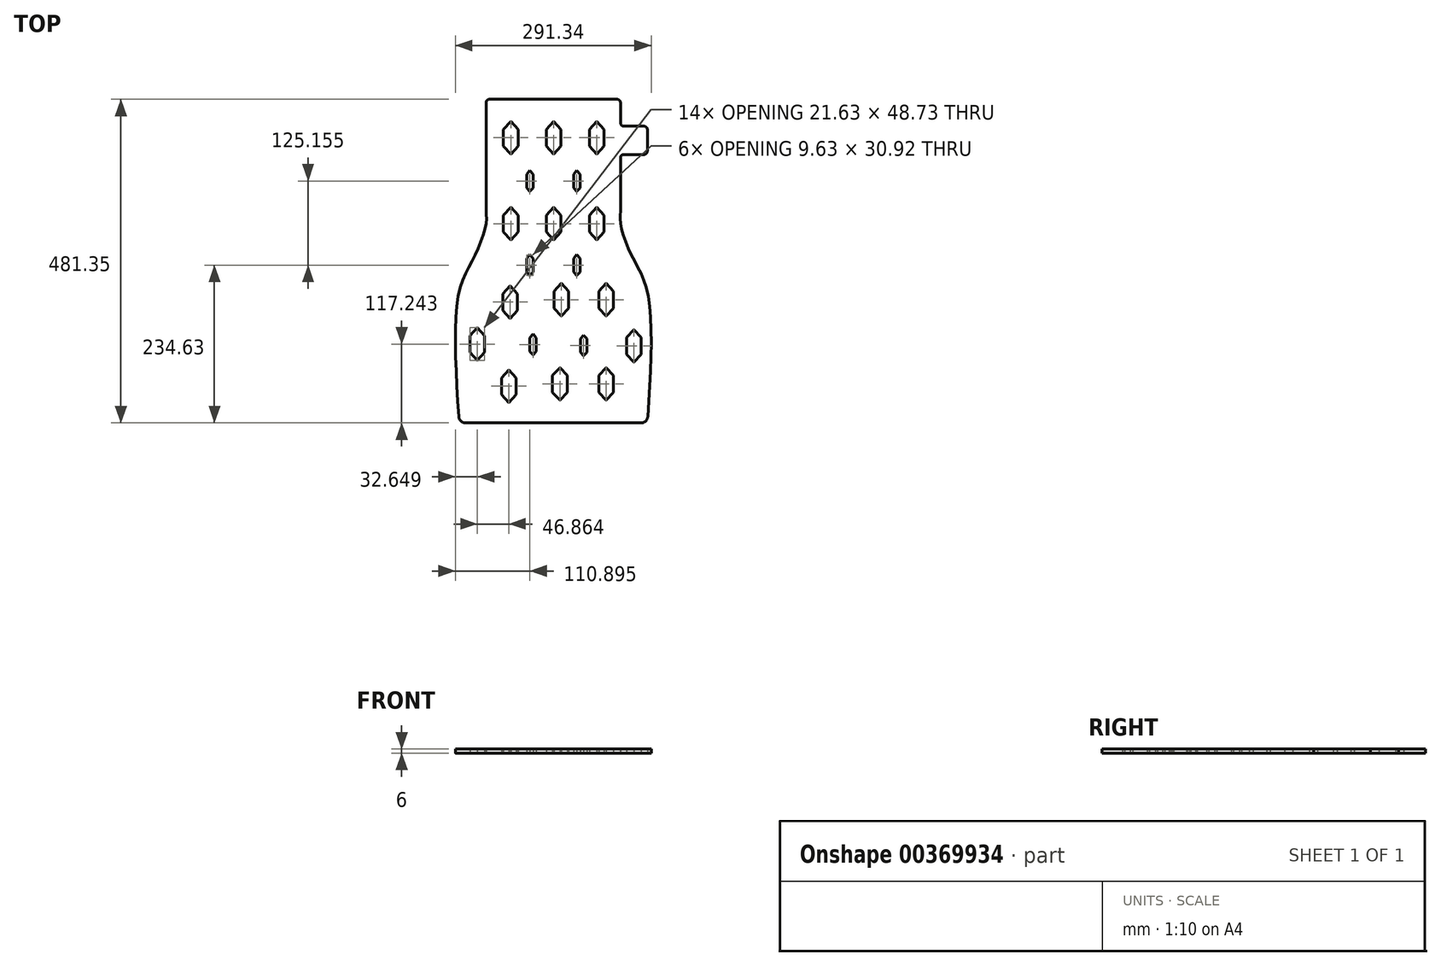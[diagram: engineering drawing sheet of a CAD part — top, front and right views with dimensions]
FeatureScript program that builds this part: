
annotation { "Feature Type Name" : "Feature", "Feature Type Description" : "" }
export const myFeature = defineFeature(function(context is Context, id is Id, definition is map)
    precondition{}
    {
        {
            var Q0;
            Q0=qCreatedBy(makeId("Top.planeOp"),FACE);
            var sketch = newSketch(context, id + "F0", { "sketchPlane" : qUnion([Q0])});
            skLineSegment(sketch, "E0", {"start": v(0, 262.18) * mm, "end": v(95, 262.18) * mm});
            skLineSegment(sketch, "E1", {"start": v(0, 262.18) * mm, "end": v(-95, 262.18) * mm});
            skLineSegment(sketch, "E2", {"start": v(130.62, -219.17) * mm, "end": v(-130.62, -219.17) * mm});
            skFitSpline(sketch, "E3", {"points": [v(-140, -219.17) * mm, v(-140, -23.78) * mm, v(-116.25, 30.48) * mm, v(-100, 77.75) * mm, v(-100, 95.38) * mm], "startDerivative": vector(-34.72, 539.25) * mm, "endDerivative": vector(-13.07, 120.29) * mm});
            skFitSpline(sketch, "E4.MirrorCS", {"points": [v(140, -219.17) * mm, v(140, -23.78) * mm, v(116.25, 30.48) * mm, v(100, 77.75) * mm, v(100, 95.38) * mm], "startDerivative": vector(34.72, 539.25) * mm, "endDerivative": vector(13.07, 120.29) * mm});
            skLineSegment(sketch, "E5", {"start": v(-100, 257.18) * mm, "end": v(-100, 95.38) * mm});
            skLineSegment(sketch, "E6", {"start": v(100, 95.38) * mm, "end": v(100, 175.09) * mm});
            skPoint(sketch, "E7.visualSharp", {"position": v(-100, 262.18) * mm});
            skArc(sketch, "E7.filletArc", {"start": v(-95, 262.18) * mm, "mid": v(-98.54, 260.72) * mm, "end": v(-100, 257.18) * mm});
            skPoint(sketch, "E8.visualSharp", {"position": v(100, 262.18) * mm});
            skArc(sketch, "E8.filletArc", {"start": v(100, 257.18) * mm, "mid": v(98.54, 260.72) * mm, "end": v(95, 262.18) * mm});
            skLineSegment(sketch, "E9", {"start": v(100, 262.18) * mm, "end": v(100, 227.18) * mm});
            skLineSegment(sketch, "E10", {"start": v(105, 222.18) * mm, "end": v(135, 222.18) * mm});
            skLineSegment(sketch, "E11", {"start": v(140, 217.18) * mm, "end": v(140, 185.09) * mm});
            skLineSegment(sketch, "E12", {"start": v(135, 180.09) * mm, "end": v(105, 180.09) * mm});
            skArc(sketch, "E13.filletArc", {"start": v(105, 180.09) * mm, "mid": v(101.46, 178.62) * mm, "end": v(100, 175.09) * mm});
            skPoint(sketch, "E14.visualSharp", {"position": v(140, 180.09) * mm});
            skArc(sketch, "E14.filletArc", {"start": v(135, 180.09) * mm, "mid": v(138.54, 181.55) * mm, "end": v(140, 185.09) * mm});
            skPoint(sketch, "E15.visualSharp", {"position": v(140, 222.18) * mm});
            skArc(sketch, "E15.filletArc", {"start": v(140, 217.18) * mm, "mid": v(138.54, 220.72) * mm, "end": v(135, 222.18) * mm});
            skPoint(sketch, "E16.visualSharp", {"position": v(100, 222.18) * mm});
            skArc(sketch, "E16.filletArc", {"start": v(100, 227.18) * mm, "mid": v(101.46, 223.65) * mm, "end": v(105, 222.18) * mm});
            skArc(sketch, "E17.filletArc", {"start": v(130.62, -219.17) * mm, "mid": v(137.46, -216.46) * mm, "end": v(140.6, -209.8) * mm});
            skArc(sketch, "E18.filletArc", {"start": v(-140.6, -209.8) * mm, "mid": v(-137.46, -216.46) * mm, "end": v(-130.62, -219.17) * mm});
            skLineSegment(sketch, "E19.left", {"start": v(-52.46, 217.58) * mm, "end": v(-52.46, 192.58) * mm});
            skLineSegment(sketch, "E19.right", {"start": v(-74.1, 217.58) * mm, "end": v(-74.1, 192.58) * mm});
            skPoint(sketch, "E20.endSnap0", {"position": v(-63.28, 136.49) * mm});
            skLineSegment(sketch, "E21", {"start": v(-63.28, 180.7) * mm, "end": v(-52.46, 192.58) * mm});
            skPoint(sketch, "E22.endSnap0", {"position": v(46.38, 56.52) * mm});
            skLineSegment(sketch, "E23.MirrorCS", {"start": v(-63.28, 229.44) * mm, "end": v(-52.46, 217.58) * mm});
            skLineSegment(sketch, "E24.MirrorCS", {"start": v(-74.1, 217.58) * mm, "end": v(-63.28, 229.44) * mm});
            skLineSegment(sketch, "E25.0.1.0", {"start": v(-74.1, 89.58) * mm, "end": v(-63.28, 101.44) * mm});
            skLineSegment(sketch, "E25.0.1.1", {"start": v(-74.1, 89.58) * mm, "end": v(-74.1, 64.58) * mm});
            skLineSegment(sketch, "E25.0.1.2", {"start": v(-74.1, 64.58) * mm, "end": v(-63.28, 52.7) * mm});
            skLineSegment(sketch, "E25.0.1.3", {"start": v(-63.28, 52.7) * mm, "end": v(-52.46, 64.58) * mm});
            skLineSegment(sketch, "E25.0.1.4", {"start": v(-52.46, 89.58) * mm, "end": v(-52.46, 64.58) * mm});
            skLineSegment(sketch, "E25.0.1.5", {"start": v(-63.28, 101.44) * mm, "end": v(-52.46, 89.58) * mm});
            skLineSegment(sketch, "E25.1.0.0", {"start": v(-10.1, 217.58) * mm, "end": v(0.72, 229.44) * mm});
            skLineSegment(sketch, "E25.1.0.1", {"start": v(-10.1, 217.58) * mm, "end": v(-10.1, 192.58) * mm});
            skLineSegment(sketch, "E25.1.0.2", {"start": v(-10.1, 192.58) * mm, "end": v(0.72, 180.7) * mm});
            skLineSegment(sketch, "E25.1.0.3", {"start": v(0.72, 180.7) * mm, "end": v(11.54, 192.58) * mm});
            skLineSegment(sketch, "E25.1.0.4", {"start": v(11.54, 217.58) * mm, "end": v(11.54, 192.58) * mm});
            skLineSegment(sketch, "E25.1.0.5", {"start": v(0.72, 229.44) * mm, "end": v(11.54, 217.58) * mm});
            skLineSegment(sketch, "E25.1.1.0", {"start": v(-10.1, 89.58) * mm, "end": v(0.72, 101.44) * mm});
            skLineSegment(sketch, "E25.1.1.1", {"start": v(-10.1, 89.58) * mm, "end": v(-10.1, 64.58) * mm});
            skLineSegment(sketch, "E25.1.1.2", {"start": v(-10.1, 64.58) * mm, "end": v(0.72, 52.7) * mm});
            skLineSegment(sketch, "E25.1.1.3", {"start": v(0.72, 52.7) * mm, "end": v(11.54, 64.58) * mm});
            skLineSegment(sketch, "E25.1.1.4", {"start": v(11.54, 89.58) * mm, "end": v(11.54, 64.58) * mm});
            skLineSegment(sketch, "E25.1.1.5", {"start": v(0.72, 101.44) * mm, "end": v(11.54, 89.58) * mm});
            skLineSegment(sketch, "E25.2.0.0", {"start": v(53.9, 217.58) * mm, "end": v(64.72, 229.44) * mm});
            skLineSegment(sketch, "E25.2.0.1", {"start": v(53.9, 217.58) * mm, "end": v(53.9, 192.58) * mm});
            skLineSegment(sketch, "E25.2.0.2", {"start": v(53.9, 192.58) * mm, "end": v(64.72, 180.7) * mm});
            skLineSegment(sketch, "E25.2.0.3", {"start": v(64.72, 180.7) * mm, "end": v(75.54, 192.58) * mm});
            skLineSegment(sketch, "E25.2.0.4", {"start": v(75.54, 217.58) * mm, "end": v(75.54, 192.58) * mm});
            skLineSegment(sketch, "E25.2.0.5", {"start": v(64.72, 229.44) * mm, "end": v(75.54, 217.58) * mm});
            skLineSegment(sketch, "E25.2.1.0", {"start": v(53.9, 89.58) * mm, "end": v(64.72, 101.44) * mm});
            skLineSegment(sketch, "E25.2.1.1", {"start": v(53.9, 89.58) * mm, "end": v(53.9, 64.58) * mm});
            skLineSegment(sketch, "E25.2.1.2", {"start": v(53.9, 64.58) * mm, "end": v(64.72, 52.7) * mm});
            skLineSegment(sketch, "E25.2.1.3", {"start": v(64.72, 52.7) * mm, "end": v(75.54, 64.58) * mm});
            skLineSegment(sketch, "E25.2.1.4", {"start": v(75.54, 89.58) * mm, "end": v(75.54, 64.58) * mm});
            skLineSegment(sketch, "E25.2.1.5", {"start": v(64.72, 101.44) * mm, "end": v(75.54, 89.58) * mm});
            skLineSegment(sketch, "E25.direction1", {"start": v(-63.28, 180.7) * mm, "end": v(0.72, 180.7) * mm, "construction": true});
            skLineSegment(sketch, "E25.direction2", {"start": v(-63.28, 180.7) * mm, "end": v(-63.28, 52.7) * mm, "construction": true});
            skLineSegment(sketch, "E26.left", {"start": v(-53.3, -26.91) * mm, "end": v(-53.3, -51.91) * mm});
            skLineSegment(sketch, "E26.right", {"start": v(-74.93, -26.91) * mm, "end": v(-74.93, -51.91) * mm});
            skLineSegment(sketch, "E27", {"start": v(-74.93, -51.91) * mm, "end": v(-64.11, -63.78) * mm});
            skLineSegment(sketch, "E28", {"start": v(-64.11, -63.78) * mm, "end": v(-53.3, -51.91) * mm});
            skLineSegment(sketch, "E29.MirrorCS", {"start": v(-64.11, -15.05) * mm, "end": v(-53.3, -26.91) * mm});
            skLineSegment(sketch, "E30.MirrorCS", {"start": v(-74.93, -26.91) * mm, "end": v(-64.11, -15.05) * mm});
            skLineSegment(sketch, "E31.0.1.0", {"start": v(-76.97, -152.13) * mm, "end": v(-66.16, -140.27) * mm});
            skLineSegment(sketch, "E31.0.1.1", {"start": v(-66.16, -140.27) * mm, "end": v(-55.34, -152.13) * mm});
            skLineSegment(sketch, "E31.0.1.2", {"start": v(-55.34, -152.13) * mm, "end": v(-55.34, -177.13) * mm});
            skLineSegment(sketch, "E31.0.1.3", {"start": v(-66.16, -189) * mm, "end": v(-55.34, -177.13) * mm});
            skLineSegment(sketch, "E31.0.1.4", {"start": v(-76.97, -177.13) * mm, "end": v(-66.16, -189) * mm});
            skLineSegment(sketch, "E31.0.1.5", {"start": v(-76.97, -152.13) * mm, "end": v(-76.97, -177.13) * mm});
            skLineSegment(sketch, "E31.1.0.0", {"start": v(1.03, -23.5) * mm, "end": v(11.84, -11.63) * mm});
            skLineSegment(sketch, "E31.1.0.1", {"start": v(11.84, -11.63) * mm, "end": v(22.66, -23.5) * mm});
            skLineSegment(sketch, "E31.1.0.2", {"start": v(22.66, -23.5) * mm, "end": v(22.66, -48.5) * mm});
            skLineSegment(sketch, "E31.1.0.3", {"start": v(11.84, -60.36) * mm, "end": v(22.66, -48.5) * mm});
            skLineSegment(sketch, "E31.1.0.4", {"start": v(1.03, -48.5) * mm, "end": v(11.84, -60.36) * mm});
            skLineSegment(sketch, "E31.1.0.5", {"start": v(1.03, -23.5) * mm, "end": v(1.03, -48.5) * mm});
            skLineSegment(sketch, "E31.1.1.0", {"start": v(-1.02, -148.72) * mm, "end": v(9.8, -136.85) * mm});
            skLineSegment(sketch, "E31.1.1.1", {"start": v(9.8, -136.85) * mm, "end": v(20.61, -148.72) * mm});
            skLineSegment(sketch, "E31.1.1.2", {"start": v(20.61, -148.72) * mm, "end": v(20.61, -173.72) * mm});
            skLineSegment(sketch, "E31.1.1.3", {"start": v(9.8, -185.58) * mm, "end": v(20.61, -173.72) * mm});
            skLineSegment(sketch, "E31.1.1.4", {"start": v(-1.02, -173.72) * mm, "end": v(9.8, -185.58) * mm});
            skLineSegment(sketch, "E31.1.1.5", {"start": v(-1.02, -148.72) * mm, "end": v(-1.02, -173.72) * mm});
            skLineSegment(sketch, "E31.direction1", {"start": v(-64.11, -63.78) * mm, "end": v(11.84, -60.36) * mm, "construction": true});
            skLineSegment(sketch, "E31.direction2", {"start": v(-64.11, -63.78) * mm, "end": v(-66.16, -189) * mm, "construction": true});
            skLineSegment(sketch, "E32.left", {"start": v(-102.2, -89.43) * mm, "end": v(-102.2, -114.43) * mm});
            skLineSegment(sketch, "E32.right", {"start": v(-123.84, -89.43) * mm, "end": v(-123.84, -114.43) * mm});
            skLineSegment(sketch, "E33", {"start": v(-123.84, -114.43) * mm, "end": v(-113.02, -126.3) * mm});
            skLineSegment(sketch, "E34", {"start": v(-113.02, -126.3) * mm, "end": v(-102.2, -114.43) * mm});
            skLineSegment(sketch, "E35.MirrorCS", {"start": v(-113.02, -77.56) * mm, "end": v(-102.2, -89.43) * mm});
            skLineSegment(sketch, "E36.MirrorCS", {"start": v(-123.84, -89.43) * mm, "end": v(-113.02, -77.56) * mm});
            skLineSegment(sketch, "E37.left", {"start": v(130.86, -92.1) * mm, "end": v(130.86, -117.1) * mm});
            skLineSegment(sketch, "E37.right", {"start": v(109.23, -92.1) * mm, "end": v(109.23, -117.1) * mm});
            skLineSegment(sketch, "E38", {"start": v(109.23, -117.1) * mm, "end": v(120.04, -128.96) * mm});
            skLineSegment(sketch, "E39", {"start": v(120.04, -128.96) * mm, "end": v(130.86, -117.1) * mm});
            skLineSegment(sketch, "E40.MirrorCS", {"start": v(120.04, -80.23) * mm, "end": v(130.86, -92.1) * mm});
            skLineSegment(sketch, "E41.MirrorCS", {"start": v(109.23, -92.1) * mm, "end": v(120.04, -80.23) * mm});
            skLineSegment(sketch, "E42.left", {"start": v(89.58, -23.5) * mm, "end": v(89.58, -48.5) * mm});
            skLineSegment(sketch, "E42.right", {"start": v(67.95, -23.5) * mm, "end": v(67.95, -48.5) * mm});
            skLineSegment(sketch, "E43", {"start": v(67.95, -48.5) * mm, "end": v(78.76, -60.36) * mm});
            skLineSegment(sketch, "E44", {"start": v(78.76, -60.36) * mm, "end": v(89.58, -48.5) * mm});
            skLineSegment(sketch, "E45.MirrorCS", {"start": v(78.76, -11.63) * mm, "end": v(89.58, -23.5) * mm});
            skLineSegment(sketch, "E46.MirrorCS", {"start": v(67.95, -23.5) * mm, "end": v(78.76, -11.63) * mm});
            skLineSegment(sketch, "E47.left", {"start": v(89.58, -148.72) * mm, "end": v(89.58, -173.72) * mm});
            skLineSegment(sketch, "E47.right", {"start": v(67.95, -148.72) * mm, "end": v(67.95, -173.72) * mm});
            skLineSegment(sketch, "E48", {"start": v(67.95, -173.72) * mm, "end": v(78.76, -185.58) * mm});
            skLineSegment(sketch, "E49", {"start": v(78.76, -185.58) * mm, "end": v(89.58, -173.72) * mm});
            skLineSegment(sketch, "E50.MirrorCS", {"start": v(78.76, -136.85) * mm, "end": v(89.58, -148.72) * mm});
            skLineSegment(sketch, "E51.MirrorCS", {"start": v(67.95, -148.72) * mm, "end": v(78.76, -136.85) * mm});
            skLineSegment(sketch, "E52", {"start": v(-74.1, 192.58) * mm, "end": v(-63.28, 180.7) * mm});
            skLineSegment(sketch, "E53.0", {"start": v(-68.1, 215.25) * mm, "end": v(-68.1, 194.9) * mm});
            skLineSegment(sketch, "E53.1", {"start": v(-63.28, 220.54) * mm, "end": v(-58.46, 215.25) * mm});
            skLineSegment(sketch, "E53.2", {"start": v(-58.46, 215.25) * mm, "end": v(-58.46, 194.9) * mm});
            skLineSegment(sketch, "E53.3", {"start": v(-68.1, 215.25) * mm, "end": v(-63.28, 220.54) * mm});
            skLineSegment(sketch, "E53.4", {"start": v(-63.28, 189.62) * mm, "end": v(-58.46, 194.9) * mm});
            skLineSegment(sketch, "E53.5", {"start": v(-68.1, 194.9) * mm, "end": v(-63.28, 189.62) * mm});
            skLineSegment(sketch, "E54.0", {"start": v(-39.6, 150.8) * mm, "end": v(-39.6, 130.44) * mm});
            skLineSegment(sketch, "E54.1", {"start": v(-34.77, 156.08) * mm, "end": v(-29.96, 150.8) * mm});
            skLineSegment(sketch, "E54.2", {"start": v(-29.96, 150.8) * mm, "end": v(-29.96, 130.44) * mm});
            skLineSegment(sketch, "E54.3", {"start": v(-39.6, 150.8) * mm, "end": v(-34.77, 156.08) * mm});
            skLineSegment(sketch, "E54.4", {"start": v(-34.77, 125.15) * mm, "end": v(-29.96, 130.44) * mm});
            skLineSegment(sketch, "E54.5", {"start": v(-39.6, 130.44) * mm, "end": v(-34.77, 125.15) * mm});
            skLineSegment(sketch, "E55.0", {"start": v(-73.1, 217.19) * mm, "end": v(-63.28, 227.96) * mm});
            skLineSegment(sketch, "E55.1", {"start": v(-73.1, 192.96) * mm, "end": v(-63.28, 182.2) * mm});
            skLineSegment(sketch, "E55.2", {"start": v(-63.28, 182.2) * mm, "end": v(-53.46, 192.96) * mm});
            skLineSegment(sketch, "E55.3", {"start": v(-73.1, 217.19) * mm, "end": v(-73.1, 192.96) * mm});
            skLineSegment(sketch, "E55.4", {"start": v(-53.46, 217.19) * mm, "end": v(-53.46, 192.96) * mm});
            skLineSegment(sketch, "E55.5", {"start": v(-63.28, 227.96) * mm, "end": v(-53.46, 217.19) * mm});
            skLineSegment(sketch, "E56.0", {"start": v(30.18, 150.8) * mm, "end": v(30.18, 130.44) * mm});
            skLineSegment(sketch, "E56.1", {"start": v(35, 156.08) * mm, "end": v(39.82, 150.8) * mm});
            skLineSegment(sketch, "E56.2", {"start": v(39.82, 150.8) * mm, "end": v(39.82, 130.44) * mm});
            skLineSegment(sketch, "E56.3", {"start": v(30.18, 150.8) * mm, "end": v(35, 156.08) * mm});
            skLineSegment(sketch, "E56.4", {"start": v(35, 125.15) * mm, "end": v(39.82, 130.44) * mm});
            skLineSegment(sketch, "E56.5", {"start": v(30.18, 130.44) * mm, "end": v(35, 125.15) * mm});
            skLineSegment(sketch, "E57.0", {"start": v(-39.6, 25.64) * mm, "end": v(-39.6, 5.28) * mm});
            skLineSegment(sketch, "E57.1", {"start": v(-34.77, 30.92) * mm, "end": v(-29.96, 25.64) * mm});
            skLineSegment(sketch, "E57.2", {"start": v(-29.96, 25.64) * mm, "end": v(-29.96, 5.28) * mm});
            skLineSegment(sketch, "E57.3", {"start": v(-39.6, 25.64) * mm, "end": v(-34.77, 30.92) * mm});
            skLineSegment(sketch, "E57.4", {"start": v(-34.77, 0) * mm, "end": v(-29.96, 5.28) * mm});
            skLineSegment(sketch, "E57.5", {"start": v(-39.6, 5.28) * mm, "end": v(-34.77, 0) * mm});
            skLineSegment(sketch, "E58.0", {"start": v(30.18, 25.64) * mm, "end": v(30.18, 5.28) * mm});
            skLineSegment(sketch, "E58.1", {"start": v(35, 30.92) * mm, "end": v(39.82, 25.64) * mm});
            skLineSegment(sketch, "E58.2", {"start": v(39.82, 25.64) * mm, "end": v(39.82, 5.28) * mm});
            skLineSegment(sketch, "E58.3", {"start": v(30.18, 25.64) * mm, "end": v(35, 30.92) * mm});
            skLineSegment(sketch, "E58.4", {"start": v(35, 0) * mm, "end": v(39.82, 5.28) * mm});
            skLineSegment(sketch, "E58.5", {"start": v(30.18, 5.28) * mm, "end": v(35, 0) * mm});
            skLineSegment(sketch, "E59.0", {"start": v(40.31, -93.85) * mm, "end": v(40.31, -114.2) * mm});
            skLineSegment(sketch, "E59.1", {"start": v(45.13, -88.57) * mm, "end": v(49.95, -93.85) * mm});
            skLineSegment(sketch, "E59.2", {"start": v(49.95, -93.85) * mm, "end": v(49.95, -114.2) * mm});
            skLineSegment(sketch, "E59.3", {"start": v(40.31, -93.85) * mm, "end": v(45.13, -88.57) * mm});
            skLineSegment(sketch, "E59.4", {"start": v(45.13, -119.5) * mm, "end": v(49.95, -114.2) * mm});
            skLineSegment(sketch, "E59.5", {"start": v(40.31, -114.2) * mm, "end": v(45.13, -119.5) * mm});
            skLineSegment(sketch, "E60.0", {"start": v(-34.96, -92.36) * mm, "end": v(-34.96, -112.72) * mm});
            skLineSegment(sketch, "E60.1", {"start": v(-30.15, -87.08) * mm, "end": v(-25.33, -92.36) * mm});
            skLineSegment(sketch, "E60.2", {"start": v(-25.33, -92.36) * mm, "end": v(-25.33, -112.72) * mm});
            skLineSegment(sketch, "E60.3", {"start": v(-34.96, -92.36) * mm, "end": v(-30.15, -87.08) * mm});
            skLineSegment(sketch, "E60.4", {"start": v(-30.15, -118) * mm, "end": v(-25.33, -112.72) * mm});
            skLineSegment(sketch, "E60.5", {"start": v(-34.96, -112.72) * mm, "end": v(-30.15, -118) * mm});
            skSolve(sketch);
        }
        {
            var Q0;
            Q0=makeQuery(id+"F0.imprint","IMPRINT",FACE,{"disambiguationData":[TD([[makeQuery(id+"F0.imprint","IMPRINT",EDGE,{"derivedFrom":sQuery(id+"F0.wireOp",EDGE,"E0")}),-1.0]])]});
            extrude(context, id + "F1", {"entities" : qUnion([Q0]), "depth" : 6 * mm, "offsetDistance" : 25 * mm});
        }
    });
